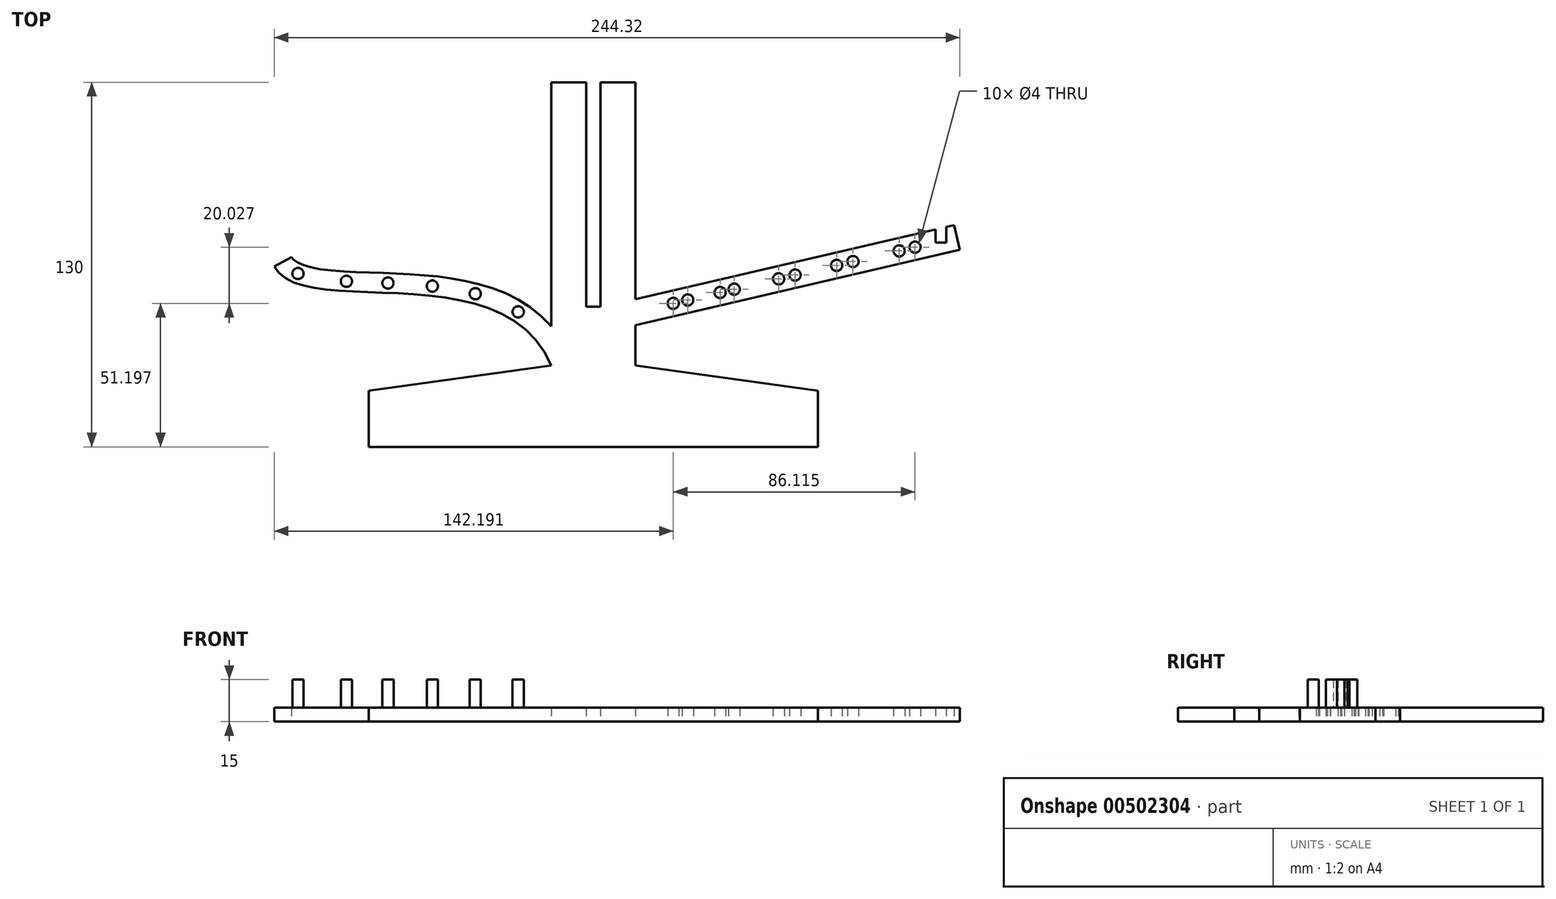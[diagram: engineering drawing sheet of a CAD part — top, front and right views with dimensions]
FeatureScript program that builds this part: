
annotation { "Feature Type Name" : "Feature", "Feature Type Description" : "" }
export const myFeature = defineFeature(function(context is Context, id is Id, definition is map)
    precondition{}
    {
        {
            var Q0;
            Q0=qCreatedBy(makeId("Top.planeOp"),FACE);
            var sketch = newSketch(context, id + "F0", { "sketchPlane" : qUnion([Q0])});
            skLineSegment(sketch, "E0", {"start": v(0, 0) * mm, "end": v(-160, 0) * mm});
            skLineSegment(sketch, "E1", {"start": v(-160, 0) * mm, "end": v(-160, 20) * mm});
            skLineSegment(sketch, "E2", {"start": v(-160, 20) * mm, "end": v(-95, 29) * mm});
            skLineSegment(sketch, "E3", {"start": v(-95, 29) * mm, "end": v(-95, 130) * mm});
            skLineSegment(sketch, "E4", {"start": v(0, 0) * mm, "end": v(0, 20) * mm});
            skLineSegment(sketch, "E5", {"start": v(0, 20) * mm, "end": v(-65, 29) * mm});
            skLineSegment(sketch, "E6", {"start": v(-65, 29) * mm, "end": v(-65, 130) * mm});
            skLineSegment(sketch, "E7", {"start": v(-95, 130) * mm, "end": v(-65, 130) * mm});
            skLineSegment(sketch, "E8", {"start": v(-82.5, 130) * mm, "end": v(-82.5, 50) * mm});
            skLineSegment(sketch, "E9", {"start": v(-82.5, 50) * mm, "end": v(-77.5, 50) * mm});
            skLineSegment(sketch, "E10", {"start": v(-77.5, 50) * mm, "end": v(-77.5, 130) * mm});
            skLineSegment(sketch, "E11", {"start": v(-77.5, 130) * mm, "end": v(-82.5, 130) * mm});
            skFitSpline(sketch, "E12", {"points": [v(-95, 29) * mm, v(-193.72, 64.34) * mm], "startDerivative": vector(-51.3, 122.64) * mm, "endDerivative": vector(-31.52, 59.05) * mm});
            skFitSpline(sketch, "E13.0", {"points": [v(-88.54, 31.7) * mm, v(-89.8, 34.71) * mm, v(-92.87, 40.23) * mm, v(-98.85, 46.9) * mm, v(-105.85, 51.99) * mm, v(-113.5, 55.69) * mm, v(-121.54, 58.26) * mm, v(-129.82, 59.97) * mm, v(-138.17, 61.03) * mm, v(-146.45, 61.65) * mm, v(-154.52, 62) * mm, v(-162.19, 62.27) * mm, v(-169.28, 62.6) * mm, v(-175.58, 63.16) * mm, v(-179.95, 63.9) * mm, v(-182.76, 64.65) * mm, v(-184.48, 65.28) * mm, v(-185.79, 65.94) * mm, v(-186.68, 66.57) * mm, v(-187.22, 67.12) * mm, v(-187.45, 67.45) * mm, v(-187.54, 67.64) * mm]});
            skLineSegment(sketch, "E14", {"start": v(-95, 29) * mm, "end": v(-95, 42.44) * mm});
            skLineSegment(sketch, "E15", {"start": v(-187.54, 67.63) * mm, "end": v(-193.72, 64.34) * mm});
            skLineSegment(sketch, "E16", {"start": v(-65, 43.4) * mm, "end": v(50.6, 70.3) * mm});
            skLineSegment(sketch, "E17", {"start": v(50.6, 70.3) * mm, "end": v(48.55, 79.13) * mm});
            skLineSegment(sketch, "E18", {"start": v(48.55, 79.13) * mm, "end": v(-65, 52.72) * mm});
            skLineSegment(sketch, "E19", {"start": v(-65, 52.72) * mm, "end": v(-65, 43.4) * mm});
            skLineSegment(sketch, "E20", {"start": v(49.57, 74.7) * mm, "end": v(-65.84, 47.87) * mm, "construction": true});
            skPoint(sketch, "E21", {"position": v(-51.53, 51.2) * mm});
            skPoint(sketch, "E22", {"position": v(-46.4, 52.4) * mm});
            skPoint(sketch, "E23", {"position": v(-34.85, 55.07) * mm});
            skPoint(sketch, "E24", {"position": v(-29.83, 56.24) * mm});
            skPoint(sketch, "E25", {"position": v(-13.99, 59.93) * mm});
            skPoint(sketch, "E26", {"position": v(-8.13, 61.29) * mm});
            skPoint(sketch, "E27", {"position": v(6.66, 64.73) * mm});
            skPoint(sketch, "E28", {"position": v(12.5, 66.09) * mm});
            skPoint(sketch, "E29", {"position": v(28.93, 69.9) * mm});
            skPoint(sketch, "E30", {"position": v(34.59, 71.22) * mm});
            skLineSegment(sketch, "E31.bottom", {"start": v(45.69, 78.46) * mm, "end": v(41.87, 78.46) * mm});
            skLineSegment(sketch, "E31.top", {"start": v(45.69, 72.92) * mm, "end": v(41.87, 72.92) * mm});
            skLineSegment(sketch, "E31.left", {"start": v(45.69, 78.46) * mm, "end": v(45.69, 72.92) * mm});
            skLineSegment(sketch, "E31.right", {"start": v(41.87, 78.46) * mm, "end": v(41.87, 72.92) * mm});
            skFitSpline(sketch, "E32.0", {"points": [v(-91.77, 30.35) * mm, v(-92.94, 33.13) * mm, v(-95.75, 38.19) * mm, v(-101.21, 44.28) * mm, v(-107.64, 48.96) * mm, v(-114.78, 52.42) * mm, v(-122.42, 54.87) * mm, v(-133.03, 57.06) * mm, v(-143.99, 58.04) * mm, v(-154.64, 58.5) * mm, v(-162.32, 58.77) * mm, v(-169.5, 59.11) * mm, v(-175.99, 59.68) * mm, v(-181.58, 60.6) * mm, v(-185.28, 61.77) * mm, v(-187.55, 62.9) * mm, v(-188.9, 63.84) * mm, v(-189.92, 64.85) * mm, v(-190.42, 65.59) * mm, v(-190.63, 65.99) * mm], "construction": true});
            skPoint(sketch, "E33", {"position": v(-106.8, 48.16) * mm});
            skPoint(sketch, "E34", {"position": v(-122.1, 54.63) * mm});
            skPoint(sketch, "E35", {"position": v(-137.36, 57.36) * mm});
            skPoint(sketch, "E36", {"position": v(-153.2, 58.44) * mm});
            skPoint(sketch, "E37", {"position": v(-167.97, 59.06) * mm});
            skPoint(sketch, "E38", {"position": v(-185.24, 61.84) * mm});
            skCircle(sketch, "E39", {"center": v(-185.24, 61.84) * mm, "radius": 2 * mm});
            skCircle(sketch, "E40", {"center": v(-167.97, 59.06) * mm, "radius": 2 * mm});
            skCircle(sketch, "E41", {"center": v(-153.2, 58.44) * mm, "radius": 2 * mm});
            skCircle(sketch, "E42", {"center": v(-137.36, 57.36) * mm, "radius": 2 * mm});
            skCircle(sketch, "E43", {"center": v(-122.1, 54.63) * mm, "radius": 2 * mm});
            skCircle(sketch, "E44", {"center": v(-106.8, 48.16) * mm, "radius": 2 * mm});
            skSolve(sketch);
        }
        {
            var Q0;
            Q0=makeQuery(id+"F0.imprint","IMPRINT",FACE,{"disambiguationData":[TD([[makeQuery(id+"F0.imprint","IMPRINT",EDGE,{"derivedFrom":sQuery(id+"F0.wireOp",EDGE,"E0")}),-1.0]])]});
            var Q1;
            {var subQ0=sQuery(id+"F0.wireOp",EDGE,"E12");Q1=makeQuery(id+"F0.imprint","IMPRINT",FACE,{"disambiguationData":[TD([[makeQuery(id+"F0.imprint","IMPRINT",EDGE,{"derivedFrom":subQ0}),-1.0]])]});}
            var Q2;
            Q2=makeQuery(id+"F0.imprint","IMPRINT",FACE,{"disambiguationData":[TD([[makeQuery(id+"F0.imprint","IMPRINT",EDGE,{"derivedFrom":sQuery(id+"F0.wireOp",EDGE,"E16")}),1.0]])]});
            extrude(context, id + "F1", {"entities" : qUnion([Q0, Q1, Q2]), "depth" : 5 * mm});
        }
        {
            var Q0;
            Q0=sQuery(id+"F0.wireOp",VERTEX,"E21");
            var Q1;
            Q1=sQuery(id+"F0.wireOp",VERTEX,"E22");
            var Q2;
            Q2=sQuery(id+"F0.wireOp",VERTEX,"E23");
            var Q3;
            Q3=sQuery(id+"F0.wireOp",VERTEX,"E24");
            var Q4;
            Q4=sQuery(id+"F0.wireOp",VERTEX,"E25");
            var Q5;
            Q5=sQuery(id+"F0.wireOp",VERTEX,"E26");
            var Q6;
            Q6=sQuery(id+"F0.wireOp",VERTEX,"E27");
            var Q7;
            Q7=sQuery(id+"F0.wireOp",VERTEX,"E28");
            var Q8;
            Q8=sQuery(id+"F0.wireOp",VERTEX,"E29");
            var Q9;
            Q9=sQuery(id+"F0.wireOp",VERTEX,"E30");
            var Q10;
            Q10=makeQuery(id+"F1.opExtrude","SWEPT_BODY",BODY,{"disambiguationData":[OSD([sQuery(id+"F0.wireOp",EDGE,"E0"),sQuery(id+"F0.wireOp",EDGE,"E1"),sQuery(id+"F0.wireOp",EDGE,"E2"),sQuery(id+"F0.wireOp",EDGE,"E3"),sQuery(id+"F0.wireOp",EDGE,"E4"),sQuery(id+"F0.wireOp",EDGE,"E5"),sQuery(id+"F0.wireOp",EDGE,"E6"),sQuery(id+"F0.wireOp",EDGE,"E7"),sQuery(id+"F0.wireOp",EDGE,"E8"),sQuery(id+"F0.wireOp",EDGE,"E9"),sQuery(id+"F0.wireOp",EDGE,"E10"),sQuery(id+"F0.wireOp",EDGE,"E12"),sQuery(id+"F0.wireOp",EDGE,"E13.0"),sQuery(id+"F0.wireOp",EDGE,"E14"),sQuery(id+"F0.wireOp",EDGE,"E15"),sQuery(id+"F0.wireOp",EDGE,"E16"),sQuery(id+"F0.wireOp",EDGE,"E17"),sQuery(id+"F0.wireOp",EDGE,"E18"),sQuery(id+"F0.wireOp",EDGE,"E31.top"),sQuery(id+"F0.wireOp",EDGE,"E31.left"),sQuery(id+"F0.wireOp",EDGE,"E31.right")])]});
            hole(context, id + "F2", {"style" : HoleStyle.SIMPLE, "endStyle" : HoleEndStyle.BLIND, "oppositeDirection" : true, "holeDiameter" : 4 * mm, "holeDepth" : 10 * mm, "isTappedThrough" : true, "tappedDepth" : 12 * mm, "tapClearance" : 3, "locations" : qUnion([Q0, Q1, Q2, Q3, Q4, Q5, Q6, Q7, Q8, Q9]), "scope" : qUnion([Q10])});
        }
        {
            var Q0;
            Q0=makeQuery(id+"F0.imprint","IMPRINT",FACE,{"disambiguationData":[TD([[makeQuery(id+"F0.imprint","IMPRINT",EDGE,{"derivedFrom":sQuery(id+"F0.wireOp",EDGE,"E44")}),1.0]])]});
            var Q1;
            Q1=makeQuery(id+"F0.imprint","IMPRINT",FACE,{"disambiguationData":[TD([[makeQuery(id+"F0.imprint","IMPRINT",EDGE,{"derivedFrom":sQuery(id+"F0.wireOp",EDGE,"E43")}),1.0]])]});
            var Q2;
            Q2=makeQuery(id+"F0.imprint","IMPRINT",FACE,{"disambiguationData":[TD([[makeQuery(id+"F0.imprint","IMPRINT",EDGE,{"derivedFrom":sQuery(id+"F0.wireOp",EDGE,"E42")}),1.0]])]});
            var Q3;
            Q3=makeQuery(id+"F0.imprint","IMPRINT",FACE,{"disambiguationData":[TD([[makeQuery(id+"F0.imprint","IMPRINT",EDGE,{"derivedFrom":sQuery(id+"F0.wireOp",EDGE,"E41")}),1.0]])]});
            var Q4;
            Q4=makeQuery(id+"F0.imprint","IMPRINT",FACE,{"disambiguationData":[TD([[makeQuery(id+"F0.imprint","IMPRINT",EDGE,{"derivedFrom":sQuery(id+"F0.wireOp",EDGE,"E40")}),1.0]])]});
            var Q5;
            Q5=makeQuery(id+"F0.imprint","IMPRINT",FACE,{"disambiguationData":[TD([[makeQuery(id+"F0.imprint","IMPRINT",EDGE,{"derivedFrom":sQuery(id+"F0.wireOp",EDGE,"E39")}),1.0]])]});
            extrude(context, id + "F3", {"entities" : qUnion([Q0, Q1, Q2, Q3, Q4, Q5]), "operationType" : NewBodyOperationType.ADD, "depth" : 15 * mm});
        }
    });
